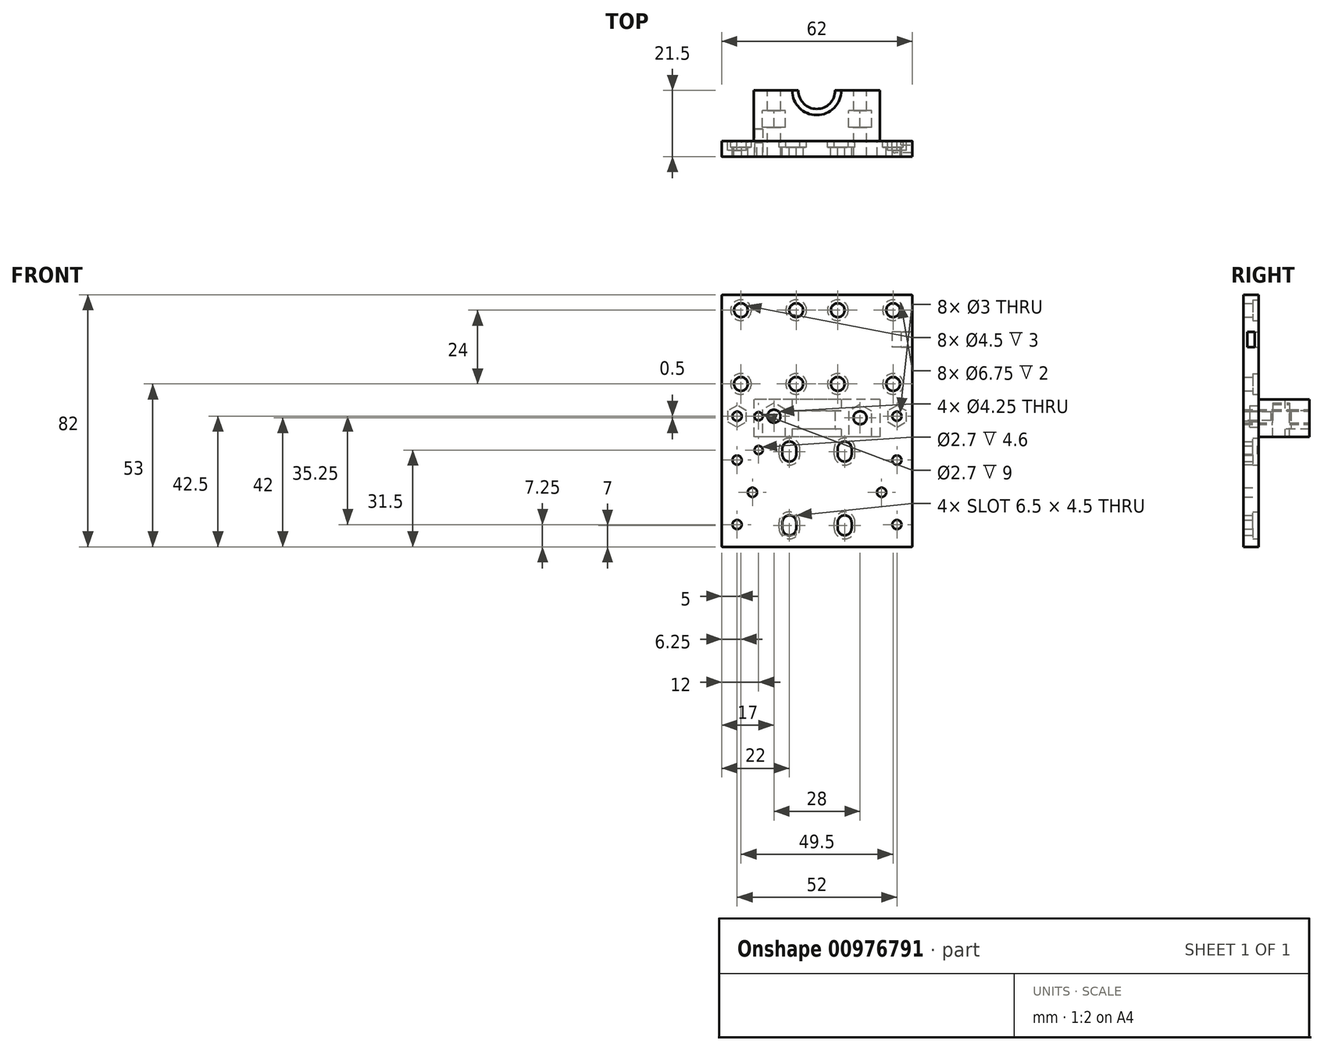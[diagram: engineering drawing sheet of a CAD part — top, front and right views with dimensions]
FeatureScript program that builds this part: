
annotation { "Feature Type Name" : "Feature", "Feature Type Description" : "" }
export const myFeature = defineFeature(function(context is Context, id is Id, definition is map)
    precondition{}
    {
        {
            var Q0;
            Q0=qCreatedBy(makeId("Front.planeOp"),FACE);
            var sketch = newSketch(context, id + "F0", { "sketchPlane" : qUnion([Q0])});
            skLineSegment(sketch, "E0", {"start": v(0, 63.1) * mm, "end": v(0, -63.33) * mm, "construction": true});
            skLineSegment(sketch, "E1", {"start": v(-65.2, 0) * mm, "end": v(78.96, 0) * mm, "construction": true});
            skPoint(sketch, "E2", {"position": v(-24.75, 0) * mm});
            skPoint(sketch, "E3", {"position": v(-6.75, 0) * mm});
            skPoint(sketch, "E4", {"position": v(-6.75, 24) * mm});
            skPoint(sketch, "E5", {"position": v(-24.75, 24) * mm});
            skPoint(sketch, "E6", {"position": v(-26, -10.5) * mm});
            skPoint(sketch, "E7", {"position": v(-19, -10.5) * mm});
            skPoint(sketch, "E8", {"position": v(-19, -21.5) * mm});
            skPoint(sketch, "E9", {"position": v(-9, -21) * mm});
            skPoint(sketch, "E10", {"position": v(-9, -23) * mm});
            skPoint(sketch, "E11", {"position": v(-9, -45) * mm});
            skPoint(sketch, "E12", {"position": v(-9, -47) * mm});
            skCircle(sketch, "E13", {"center": v(-26, -10.5) * mm, "radius": 1.35 * mm});
            skCircle(sketch, "E14", {"center": v(-19, -10.5) * mm, "radius": 1.35 * mm});
            skCircle(sketch, "E15", {"center": v(-19, -21.5) * mm, "radius": 1.35 * mm});
            skCircle(sketch, "E16", {"center": v(-24.75, 24) * mm, "radius": 2.25 * mm});
            skCircle(sketch, "E17", {"center": v(-6.75, 24) * mm, "radius": 2.25 * mm});
            skCircle(sketch, "E18", {"center": v(-24.75, 0) * mm, "radius": 2.25 * mm});
            skCircle(sketch, "E19", {"center": v(-6.75, 0) * mm, "radius": 2.25 * mm});
            skArc(sketch, "E20", {"start": v(-6.75, -21) * mm, "mid": v(-9, -18.75) * mm, "end": v(-11.25, -21) * mm});
            skArc(sketch, "E21", {"start": v(-11.25, -23) * mm, "mid": v(-9, -25.25) * mm, "end": v(-6.75, -23) * mm});
            skLineSegment(sketch, "E22", {"start": v(-6.75, -23) * mm, "end": v(-6.75, -21) * mm});
            skLineSegment(sketch, "E23", {"start": v(-11.25, -23) * mm, "end": v(-11.25, -21) * mm});
            skArc(sketch, "E24", {"start": v(-6.75, -45) * mm, "mid": v(-9, -42.75) * mm, "end": v(-11.25, -45) * mm});
            skArc(sketch, "E25", {"start": v(-11.25, -47) * mm, "mid": v(-9, -49.25) * mm, "end": v(-6.75, -47) * mm});
            skLineSegment(sketch, "E26", {"start": v(-6.75, -47) * mm, "end": v(-6.75, -45) * mm});
            skLineSegment(sketch, "E27", {"start": v(-11.25, -47) * mm, "end": v(-11.25, -45) * mm});
            skLineSegment(sketch, "E28.MirrorCS", {"start": v(11.25, -47) * mm, "end": v(11.25, -45) * mm});
            skLineSegment(sketch, "E29.MirrorCS", {"start": v(11.25, -23) * mm, "end": v(11.25, -21) * mm});
            skArc(sketch, "E30.MirrorCS", {"start": v(11.25, -47) * mm, "mid": v(9, -49.25) * mm, "end": v(6.75, -47) * mm});
            skCircle(sketch, "E31.MirrorC", {"center": v(19, -21.5) * mm, "radius": 1.35 * mm});
            skCircle(sketch, "E32.MirrorC", {"center": v(19, -10.5) * mm, "radius": 1.35 * mm});
            skLineSegment(sketch, "E33.MirrorCS", {"start": v(6.75, -23) * mm, "end": v(6.75, -21) * mm});
            skLineSegment(sketch, "E34.MirrorCS", {"start": v(6.75, -47) * mm, "end": v(6.75, -45) * mm});
            skCircle(sketch, "E35.MirrorC", {"center": v(26, -10.5) * mm, "radius": 1.35 * mm});
            skCircle(sketch, "E36.MirrorC", {"center": v(6.75, 24) * mm, "radius": 2.25 * mm});
            skCircle(sketch, "E37.MirrorC", {"center": v(24.75, 0) * mm, "radius": 2.25 * mm});
            skArc(sketch, "E38.MirrorCS", {"start": v(6.75, -45) * mm, "mid": v(9, -42.75) * mm, "end": v(11.25, -45) * mm});
            skCircle(sketch, "E39.MirrorC", {"center": v(6.75, 0) * mm, "radius": 2.25 * mm});
            skArc(sketch, "E40.MirrorCS", {"start": v(6.75, -21) * mm, "mid": v(9, -18.75) * mm, "end": v(11.25, -21) * mm});
            skArc(sketch, "E41.MirrorCS", {"start": v(11.25, -23) * mm, "mid": v(9, -25.25) * mm, "end": v(6.75, -23) * mm});
            skCircle(sketch, "E42.MirrorC", {"center": v(24.75, 24) * mm, "radius": 2.25 * mm});
            skArc(sketch, "E43.0", {"start": v(5.62, -21) * mm, "mid": v(9, -17.62) * mm, "end": v(12.37, -21) * mm});
            skLineSegment(sketch, "E43.1", {"start": v(5.63, -23) * mm, "end": v(5.63, -21) * mm});
            skArc(sketch, "E43.2", {"start": v(12.37, -23) * mm, "mid": v(9, -26.38) * mm, "end": v(5.62, -23) * mm});
            skLineSegment(sketch, "E43.3", {"start": v(12.38, -23) * mm, "end": v(12.38, -21) * mm});
            skArc(sketch, "E44.0", {"start": v(5.62, -45) * mm, "mid": v(9, -41.62) * mm, "end": v(12.37, -45) * mm});
            skLineSegment(sketch, "E44.1", {"start": v(5.63, -47) * mm, "end": v(5.63, -45) * mm});
            skArc(sketch, "E44.2", {"start": v(12.37, -47) * mm, "mid": v(9, -50.38) * mm, "end": v(5.62, -47) * mm});
            skLineSegment(sketch, "E44.3", {"start": v(12.38, -47) * mm, "end": v(12.38, -45) * mm});
            skArc(sketch, "E45.0", {"start": v(-5.62, -21) * mm, "mid": v(-9, -17.62) * mm, "end": v(-12.37, -21) * mm});
            skLineSegment(sketch, "E45.1", {"start": v(-5.62, -23) * mm, "end": v(-5.62, -21) * mm});
            skArc(sketch, "E45.2", {"start": v(-12.37, -23) * mm, "mid": v(-9, -26.38) * mm, "end": v(-5.62, -23) * mm});
            skLineSegment(sketch, "E45.3", {"start": v(-12.37, -23) * mm, "end": v(-12.37, -21) * mm});
            skArc(sketch, "E46.0", {"start": v(-5.62, -45) * mm, "mid": v(-9, -41.62) * mm, "end": v(-12.37, -45) * mm});
            skLineSegment(sketch, "E46.1", {"start": v(-5.62, -47) * mm, "end": v(-5.62, -45) * mm});
            skArc(sketch, "E46.2", {"start": v(-12.37, -47) * mm, "mid": v(-9, -50.38) * mm, "end": v(-5.62, -47) * mm});
            skLineSegment(sketch, "E46.3", {"start": v(-12.37, -47) * mm, "end": v(-12.37, -45) * mm});
            skPoint(sketch, "E47", {"position": v(26, -24.75) * mm});
            skPoint(sketch, "E48", {"position": v(21, -35.25) * mm});
            skPoint(sketch, "E49", {"position": v(26, -45.75) * mm});
            skPoint(sketch, "E50.MirrorP", {"position": v(-26, -24.75) * mm});
            skPoint(sketch, "E51.MirrorP", {"position": v(-21, -35.25) * mm});
            skPoint(sketch, "E52.MirrorP", {"position": v(-26, -45.75) * mm});
            skSolve(sketch);
        }
        {
            var Q0;
            Q0=qCreatedBy(makeId("Front.planeOp"),FACE);
            var sketch = newSketch(context, id + "F1", { "sketchPlane" : qUnion([Q0])});
            skLineSegment(sketch, "E53.bottom", {"start": v(0, 29) * mm, "end": v(-31, 29) * mm});
            skLineSegment(sketch, "E53.top", {"start": v(0, -53) * mm, "end": v(-31, -53) * mm});
            skLineSegment(sketch, "E53.left", {"start": v(0, 29) * mm, "end": v(0, -53) * mm});
            skLineSegment(sketch, "E53.right", {"start": v(-31, 29) * mm, "end": v(-31, -53) * mm});
            skLineSegment(sketch, "E54.MirrorCS", {"start": v(0, -53) * mm, "end": v(31, -53) * mm});
            skLineSegment(sketch, "E55.MirrorCS", {"start": v(31, 29) * mm, "end": v(31, -53) * mm});
            skLineSegment(sketch, "E56.MirrorCS", {"start": v(0, 29) * mm, "end": v(31, 29) * mm});
            skSolve(sketch);
        }
        {
            var Q0;
            Q0 = qSketchRegion(id + "F1", true);
            extrude(context, id + "F2", {"entities" : qUnion([Q0]), "depth" : 5 * mm, "offsetDistance" : 25 * mm});
        }
        {
            var Q0;
            Q0=sQuery(id+"F0.wireOp",VERTEX,"E42.MirrorC.center");
            var Q1;
            Q1=sQuery(id+"F0.wireOp",VERTEX,"E36.MirrorC.center");
            var Q2;
            Q2=sQuery(id+"F0.wireOp",VERTEX,"E4");
            var Q3;
            Q3=sQuery(id+"F0.wireOp",VERTEX,"E5");
            var Q4;
            Q4=sQuery(id+"F0.wireOp",VERTEX,"E2");
            var Q5;
            Q5=sQuery(id+"F0.wireOp",VERTEX,"E3");
            var Q6;
            Q6=sQuery(id+"F0.wireOp",VERTEX,"E39.MirrorC.center");
            var Q7;
            Q7=sQuery(id+"F0.wireOp",VERTEX,"E37.MirrorC.center");
            var Q8;
            Q8=makeQuery(id+"F2.opExtrude","SWEPT_BODY",BODY,{"disambiguationData":[OSD([sQuery(id+"F1.wireOp",EDGE,"E53.bottom"),sQuery(id+"F1.wireOp",EDGE,"E53.top"),sQuery(id+"F1.wireOp",EDGE,"E53.right"),sQuery(id+"F1.wireOp",EDGE,"E54.MirrorCS"),sQuery(id+"F1.wireOp",EDGE,"E55.MirrorCS"),sQuery(id+"F1.wireOp",EDGE,"E56.MirrorCS")])]});
            hole(context, id + "F3", {"style" : HoleStyle.C_BORE, "endStyle" : HoleEndStyle.THROUGH, "oppositeDirection" : true, "holeDiameter" : 4.5 * mm, "cBoreDiameter" : 6.75 * mm, "cBoreDepth" : 2 * mm, "majorDiameter" : 5 * mm, "isTappedThrough" : true, "tappedDepth" : 15 * mm, "tapClearance" : 3, "locations" : qUnion([Q0, Q1, Q2, Q3, Q4, Q5, Q6, Q7]), "scope" : qUnion([Q8])});
        }
        {
            var Q0;
            Q0=makeQuery(id+"F0.imprint","IMPRINT",FACE,{"disambiguationData":[TD([[makeQuery(id+"F0.imprint","IMPRINT",EDGE,{"derivedFrom":sQuery(id+"F0.wireOp",EDGE,"E29.MirrorCS")}),1.0]])]});
            var Q1;
            Q1=makeQuery(id+"F0.imprint","IMPRINT",FACE,{"disambiguationData":[TD([[makeQuery(id+"F0.imprint","IMPRINT",EDGE,{"derivedFrom":sQuery(id+"F0.wireOp",EDGE,"E20")}),1.0]])]});
            var Q2;
            Q2=makeQuery(id+"F0.imprint","IMPRINT",FACE,{"disambiguationData":[TD([[makeQuery(id+"F0.imprint","IMPRINT",EDGE,{"derivedFrom":sQuery(id+"F0.wireOp",EDGE,"E28.MirrorCS")}),1.0]])]});
            var Q3;
            Q3=makeQuery(id+"F0.imprint","IMPRINT",FACE,{"disambiguationData":[TD([[makeQuery(id+"F0.imprint","IMPRINT",EDGE,{"derivedFrom":sQuery(id+"F0.wireOp",EDGE,"E24")}),1.0]])]});
            extrude(context, id + "F4", {"entities" : qUnion([Q0, Q1, Q2, Q3]), "operationType" : NewBodyOperationType.REMOVE, "endBound" : BoundingType.UP_TO_NEXT, "depth" : 25 * mm, "offsetDistance" : 25 * mm});
        }
        {
            var Q0;
            Q0=makeQuery(id+"F0.imprint","IMPRINT",FACE,{"disambiguationData":[TD([[makeQuery(id+"F0.imprint","IMPRINT",EDGE,{"derivedFrom":sQuery(id+"F0.wireOp",EDGE,"E29.MirrorCS")}),-1.0]])]});
            var Q1;
            Q1=makeQuery(id+"F0.imprint","IMPRINT",FACE,{"disambiguationData":[TD([[makeQuery(id+"F0.imprint","IMPRINT",EDGE,{"derivedFrom":sQuery(id+"F0.wireOp",EDGE,"E20")}),-1.0]])]});
            var Q2;
            Q2=makeQuery(id+"F0.imprint","IMPRINT",FACE,{"disambiguationData":[TD([[makeQuery(id+"F0.imprint","IMPRINT",EDGE,{"derivedFrom":sQuery(id+"F0.wireOp",EDGE,"E24")}),-1.0]])]});
            var Q3;
            Q3=makeQuery(id+"F0.imprint","IMPRINT",FACE,{"disambiguationData":[TD([[makeQuery(id+"F0.imprint","IMPRINT",EDGE,{"derivedFrom":sQuery(id+"F0.wireOp",EDGE,"E28.MirrorCS")}),-1.0]])]});
            extrude(context, id + "F5", {"entities" : qUnion([Q0, Q1, Q2, Q3]), "operationType" : NewBodyOperationType.REMOVE, "depth" : 2 * mm, "offsetDistance" : 25 * mm});
        }
        {
            var Q0;
            Q0=makeQuery(id+"F0.imprint","IMPRINT",FACE,{"disambiguationData":[TD([[makeQuery(id+"F0.imprint","IMPRINT",EDGE,{"derivedFrom":sQuery(id+"F0.wireOp",EDGE,"E15")}),1.0]])]});
            var Q1;
            Q1=makeQuery(id+"F0.imprint","IMPRINT",FACE,{"disambiguationData":[TD([[makeQuery(id+"F0.imprint","IMPRINT",EDGE,{"derivedFrom":sQuery(id+"F0.wireOp",EDGE,"E31.MirrorC")}),-1.0]])]});
            var Q2;
            Q2=sQuery(id+"F0.wireOp",EDGE,"E35.MirrorC");
            var Q3;
            Q3=sQuery(id+"F0.wireOp",EDGE,"E32.MirrorC");
            var Q4;
            Q4=sQuery(id+"F0.wireOp",EDGE,"E31.MirrorC");
            var Q5;
            Q5=sQuery(id+"F0.wireOp",EDGE,"E15");
            var Q6;
            Q6=sQuery(id+"F0.wireOp",EDGE,"E14");
            var Q7;
            Q7=sQuery(id+"F0.wireOp",EDGE,"E13");
            extrude(context, id + "F6", {"entities" : qUnion([Q0, Q1]), "operationType" : NewBodyOperationType.REMOVE, "surfaceEntities" : qUnion([Q2, Q3, Q4, Q5, Q6, Q7]), "endBound" : BoundingType.THROUGH_ALL, "depth" : 1 * mm, "offsetDistance" : 25 * mm, "hasSecondDirection" : true, "secondDirectionOppositeDirection" : false, "secondDirectionDepth" : 0.4 * mm});
        }
        {
            var Q0;
            Q0=sQuery(id+"F0.wireOp",VERTEX,"E35.MirrorC.center");
            var Q1;
            Q1=sQuery(id+"F0.wireOp",VERTEX,"E6");
            var Q2;
            Q2=makeQuery(id+"F2.opExtrude","SWEPT_BODY",BODY,{"disambiguationData":[OSD([sQuery(id+"F1.wireOp",EDGE,"E53.bottom"),sQuery(id+"F1.wireOp",EDGE,"E53.top"),sQuery(id+"F1.wireOp",EDGE,"E53.right"),sQuery(id+"F1.wireOp",EDGE,"E54.MirrorCS"),sQuery(id+"F1.wireOp",EDGE,"E55.MirrorCS"),sQuery(id+"F1.wireOp",EDGE,"E56.MirrorCS")])]});
            hole(context, id + "F7", {"style" : HoleStyle.SIMPLE, "endStyle" : HoleEndStyle.THROUGH, "oppositeDirection" : true, "holeDiameter" : 3 * mm, "majorDiameter" : 5 * mm, "isTappedThrough" : true, "tappedDepth" : 15 * mm, "tapClearance" : 3, "locations" : qUnion([Q0, Q1]), "scope" : qUnion([Q2])});
        }
        {
            var Q0;
            Q0=makeQuery(id+"F2.opExtrude","CAP_FACE",FACE,{"disambiguationData":[OSD([sQuery(id+"F1.wireOp",EDGE,"E53.bottom"),sQuery(id+"F1.wireOp",EDGE,"E53.top"),sQuery(id+"F1.wireOp",EDGE,"E53.right"),sQuery(id+"F1.wireOp",EDGE,"E54.MirrorCS"),sQuery(id+"F1.wireOp",EDGE,"E55.MirrorCS"),sQuery(id+"F1.wireOp",EDGE,"E56.MirrorCS")])],"isStart":true});
            var sketch = newSketch(context, id + "F8", { "sketchPlane" : qUnion([Q0])});
            skPoint(sketch, "E57.0", {"position": v(-26, -10.5) * mm});
            skPoint(sketch, "E58.0", {"position": v(26, -10.5) * mm});
            skCircle(sketch, "E59.cCircle", {"center": v(-26, -10.5) * mm, "radius": 3.02 * mm, "construction": true});
            skLineSegment(sketch, "E59.0", {"start": v(-22.97, -8.75) * mm, "end": v(-22.97, -12.25) * mm});
            skLineSegment(sketch, "E59.1", {"start": v(-22.97, -12.25) * mm, "end": v(-26, -14) * mm});
            skLineSegment(sketch, "E59.2", {"start": v(-26, -14) * mm, "end": v(-29.02, -12.25) * mm});
            skLineSegment(sketch, "E59.3", {"start": v(-29.02, -12.25) * mm, "end": v(-29.02, -8.75) * mm});
            skLineSegment(sketch, "E59.4", {"start": v(-29.02, -8.75) * mm, "end": v(-26, -7) * mm});
            skLineSegment(sketch, "E59.5", {"start": v(-26, -7) * mm, "end": v(-22.97, -8.75) * mm});
            skPoint(sketch, "E59.0.midPoint", {"position": v(-22.97, -10.5) * mm});
            skCircle(sketch, "E60.cCircle", {"center": v(26, -10.5) * mm, "radius": 3.02 * mm, "construction": true});
            skLineSegment(sketch, "E60.0", {"start": v(29.02, -8.75) * mm, "end": v(29.02, -12.25) * mm});
            skLineSegment(sketch, "E60.1", {"start": v(29.02, -12.25) * mm, "end": v(26, -14) * mm});
            skLineSegment(sketch, "E60.2", {"start": v(26, -14) * mm, "end": v(22.97, -12.25) * mm});
            skLineSegment(sketch, "E60.3", {"start": v(22.97, -12.25) * mm, "end": v(22.97, -8.75) * mm});
            skLineSegment(sketch, "E60.4", {"start": v(22.97, -8.75) * mm, "end": v(26, -7) * mm});
            skLineSegment(sketch, "E60.5", {"start": v(26, -7) * mm, "end": v(29.02, -8.75) * mm});
            skPoint(sketch, "E60.0.midPoint", {"position": v(29.02, -10.5) * mm});
            skSolve(sketch);
        }
        {
            var Q0;
            Q0=makeQuery(id+"F8.imprint","IMPRINT",FACE,{"disambiguationData":[TD([[makeQuery(id+"F8.imprint","IMPRINT",EDGE,{"derivedFrom":sQuery(id+"F8.wireOp",EDGE,"E60.0")}),-1.0]])]});
            var Q1;
            Q1=makeQuery(id+"F8.imprint","IMPRINT",FACE,{"disambiguationData":[TD([[makeQuery(id+"F8.imprint","IMPRINT",EDGE,{"derivedFrom":sQuery(id+"F8.wireOp",EDGE,"E59.0")}),-1.0]])]});
            extrude(context, id + "F9", {"entities" : qUnion([Q0, Q1]), "operationType" : NewBodyOperationType.REMOVE, "oppositeDirection" : true, "depth" : 3 * mm, "offsetDistance" : 25 * mm});
        }
        {
            var Q0;
            Q0=makeQuery(id+"F2.opExtrude","CAP_FACE",FACE,{"disambiguationData":[OSD([sQuery(id+"F1.wireOp",EDGE,"E53.bottom"),sQuery(id+"F1.wireOp",EDGE,"E53.top"),sQuery(id+"F1.wireOp",EDGE,"E53.right"),sQuery(id+"F1.wireOp",EDGE,"E54.MirrorCS"),sQuery(id+"F1.wireOp",EDGE,"E55.MirrorCS"),sQuery(id+"F1.wireOp",EDGE,"E56.MirrorCS")])],"isStart":true});
            var sketch = newSketch(context, id + "F10", { "sketchPlane" : qUnion([Q0])});
            skLineSegment(sketch, "E61.bottom", {"start": v(-20.4, -5) * mm, "end": v(0.1, -5) * mm});
            skLineSegment(sketch, "E61.top", {"start": v(-20.4, -17.25) * mm, "end": v(-7.9, -17.25) * mm});
            skLineSegment(sketch, "E61.left", {"start": v(-20.4, -5) * mm, "end": v(-20.4, -17.25) * mm});
            skLineSegment(sketch, "E61.right", {"start": v(20.6, -5) * mm, "end": v(20.6, -17.25) * mm});
            skLineSegment(sketch, "E62", {"start": v(0.1, -2.78) * mm, "end": v(0.1, -28.46) * mm, "construction": true});
            skLineSegment(sketch, "E63", {"start": v(-7.9, -5) * mm, "end": v(-7.9, -8.7) * mm});
            skLineSegment(sketch, "E64", {"start": v(-7.9, -8.7) * mm, "end": v(-5.9, -8.7) * mm});
            skLineSegment(sketch, "E65", {"start": v(-5.9, -8.7) * mm, "end": v(-5.9, -14.7) * mm});
            skLineSegment(sketch, "E66", {"start": v(-5.9, -14.7) * mm, "end": v(-7.9, -14.7) * mm});
            skLineSegment(sketch, "E67", {"start": v(-7.9, -14.7) * mm, "end": v(-7.9, -17.25) * mm});
            skLineSegment(sketch, "E68", {"start": v(1.38, -5) * mm, "end": v(20.6, -5) * mm});
            skLineSegment(sketch, "E69", {"start": v(0.1, -5) * mm, "end": v(1.38, -5) * mm});
            skLineSegment(sketch, "E70", {"start": v(0.1, -17.25) * mm, "end": v(20.6, -17.25) * mm});
            skLineSegment(sketch, "E71", {"start": v(-7.9, -17.25) * mm, "end": v(0.1, -17.25) * mm});
            skSolve(sketch);
        }
        {
            var Q0;
            Q0=makeQuery(id+"F10.imprint","IMPRINT",FACE,{"disambiguationData":[TD([[makeQuery(id+"F10.imprint","IMPRINT",EDGE,{"derivedFrom":sQuery(id+"F10.wireOp",EDGE,"E61.top")}),1.0]])]});
            var Q1;
            Q1=makeQuery(id+"F10.imprint","IMPRINT",FACE,{"disambiguationData":[TD([[makeQuery(id+"F10.imprint","IMPRINT",EDGE,{"derivedFrom":sQuery(id+"F10.wireOp",EDGE,"E61.right")}),-1.0]])]});
            extrude(context, id + "F11", {"entities" : qUnion([Q0, Q1]), "operationType" : NewBodyOperationType.ADD, "depth" : 16.5 * mm, "offsetDistance" : 25 * mm});
        }
        {
            var Q0;
            Q0=makeQuery(id+"F11.opExtrude","CAP_FACE",FACE,{"disambiguationData":[OSD([sQuery(id+"F10.wireOp",EDGE,"E61.bottom"),sQuery(id+"F10.wireOp",EDGE,"E61.top"),sQuery(id+"F10.wireOp",EDGE,"E61.left"),sQuery(id+"F10.wireOp",EDGE,"E61.right"),sQuery(id+"F10.wireOp",EDGE,"E68"),sQuery(id+"F10.wireOp",EDGE,"E69"),sQuery(id+"F10.wireOp",EDGE,"E70"),sQuery(id+"F10.wireOp",EDGE,"E71")])],"isStart":false});
            var sketch = newSketch(context, id + "F12", { "sketchPlane" : qUnion([Q0])});
            skLineSegment(sketch, "E72.0", {"start": v(-20.4, -5) * mm, "end": v(-20.4, -17.25) * mm});
            skLineSegment(sketch, "E73.0", {"start": v(20.6, -5) * mm, "end": v(20.6, -17.25) * mm});
            skLineSegment(sketch, "E74", {"start": v(0.1, -3.2) * mm, "end": v(0.1, -20.42) * mm, "construction": true});
            skLineSegment(sketch, "E75", {"start": v(0.1, -5) * mm, "end": v(-7.9, -5) * mm});
            skLineSegment(sketch, "E76", {"start": v(-7.9, -5) * mm, "end": v(-7.9, -8.7) * mm});
            skLineSegment(sketch, "E77", {"start": v(-7.9, -8.7) * mm, "end": v(-5.9, -8.7) * mm});
            skLineSegment(sketch, "E78", {"start": v(-5.9, -8.7) * mm, "end": v(-5.9, -14.7) * mm});
            skLineSegment(sketch, "E79", {"start": v(-5.9, -14.7) * mm, "end": v(-7.9, -14.7) * mm});
            skLineSegment(sketch, "E80", {"start": v(-7.9, -14.7) * mm, "end": v(-7.9, -17.25) * mm});
            skLineSegment(sketch, "E81", {"start": v(-7.9, -17.25) * mm, "end": v(0.1, -17.25) * mm});
            skLineSegment(sketch, "E82", {"start": v(0.1, -5) * mm, "end": v(0.1, -17.25) * mm});
            skSolve(sketch);
        }
        {
            var Q0;
            Q0=makeQuery(id+"F12.imprint","IMPRINT",FACE,{"disambiguationData":[TD([[makeQuery(id+"F12.imprint","IMPRINT",EDGE,{"derivedFrom":sQuery(id+"F12.wireOp",EDGE,"E75")}),-1.0]])]});
            var Q1;
            Q1=sQuery(id+"F12.wireOp",EDGE,"E74");
            revolve(context, id + "F13", {"operationType" : NewBodyOperationType.REMOVE, "surfaceOperationType" : NewSurfaceOperationType.NEW, "entities" : qUnion([Q0]), "axis" : qUnion([Q1]), "revolveType" : RevolveType.FULL, "oppositeDirection" : true});
        }
        {
            var Q0;
            {var subQ0=sQuery(id+"F10.wireOp",EDGE,"E61.left");var subQ1=sQuery(id+"F10.wireOp",EDGE,"E71");var subQ2=sQuery(id+"F10.wireOp",EDGE,"E70");var subQ3=sQuery(id+"F10.wireOp",EDGE,"E61.top");var subQ4=sQuery(id+"F10.wireOp",EDGE,"E69");var subQ5=sQuery(id+"F10.wireOp",EDGE,"E68");var subQ6=sQuery(id+"F10.wireOp",EDGE,"E61.bottom");Q0=makeQuery(id+"F13.boolean.opBoolean","SPLIT",FACE,{"disambiguationData":[TD([makeQuery(id+"F11.opExtrude","SWEPT_FACE",FACE,{"disambiguationData":[OSD([subQ0])]})])],"derivedFrom":makeQuery(id+"F11.opExtrude","CAP_FACE",FACE,{"disambiguationData":[OSD([subQ6,subQ3,subQ0,sQuery(id+"F10.wireOp",EDGE,"E61.right"),subQ5,subQ4,subQ2,subQ1])],"isStart":false})});}
            var sketch = newSketch(context, id + "F14", { "sketchPlane" : qUnion([Q0])});
            skPoint(sketch, "E83", {"position": v(-14, -11) * mm});
            skPoint(sketch, "E84", {"position": v(14, -10.5) * mm});
            skSolve(sketch);
        }
        {
            var Q0;
            Q0=sQuery(id+"F14.wireOp",VERTEX,"E83");
            var Q1;
            Q1=sQuery(id+"F14.wireOp",VERTEX,"E84");
            var Q2;
            Q2=makeQuery(id+"F2.opExtrude","SWEPT_BODY",BODY,{"disambiguationData":[OSD([sQuery(id+"F1.wireOp",EDGE,"E53.bottom"),sQuery(id+"F1.wireOp",EDGE,"E53.top"),sQuery(id+"F1.wireOp",EDGE,"E53.right"),sQuery(id+"F1.wireOp",EDGE,"E54.MirrorCS"),sQuery(id+"F1.wireOp",EDGE,"E55.MirrorCS"),sQuery(id+"F1.wireOp",EDGE,"E56.MirrorCS")])]});
            hole(context, id + "F15", {"style" : HoleStyle.SIMPLE, "endStyle" : HoleEndStyle.THROUGH, "holeDiameter" : 4.25 * mm, "majorDiameter" : 5 * mm, "isTappedThrough" : true, "tappedDepth" : 15 * mm, "tapClearance" : 3, "locations" : qUnion([Q0, Q1]), "scope" : qUnion([Q2])});
        }
        {
            var Q0;
            Q0=sQuery(id+"F0.wireOp",VERTEX,"E47");
            var Q1;
            Q1=sQuery(id+"F0.wireOp",VERTEX,"E48");
            var Q2;
            Q2=sQuery(id+"F0.wireOp",VERTEX,"E49");
            var Q3;
            Q3=sQuery(id+"F0.wireOp",VERTEX,"E51.MirrorP");
            var Q4;
            Q4=sQuery(id+"F0.wireOp",VERTEX,"E50.MirrorP");
            var Q5;
            Q5=sQuery(id+"F0.wireOp",VERTEX,"E52.MirrorP");
            var Q6;
            Q6=makeQuery(id+"F2.opExtrude","SWEPT_BODY",BODY,{"disambiguationData":[OSD([sQuery(id+"F1.wireOp",EDGE,"E53.bottom"),sQuery(id+"F1.wireOp",EDGE,"E53.top"),sQuery(id+"F1.wireOp",EDGE,"E53.right"),sQuery(id+"F1.wireOp",EDGE,"E54.MirrorCS"),sQuery(id+"F1.wireOp",EDGE,"E55.MirrorCS"),sQuery(id+"F1.wireOp",EDGE,"E56.MirrorCS")])]});
            hole(context, id + "F16", {"style" : HoleStyle.SIMPLE, "endStyle" : HoleEndStyle.THROUGH, "oppositeDirection" : true, "holeDiameter" : 3 * mm, "majorDiameter" : 5 * mm, "isTappedThrough" : true, "tappedDepth" : 15 * mm, "tapClearance" : 3, "locations" : qUnion([Q0, Q1, Q2, Q3, Q4, Q5]), "scope" : qUnion([Q6])});
        }
        {
            var Q0;
            {var subQ0=sQuery(id+"F10.wireOp",EDGE,"E61.left");var subQ1=sQuery(id+"F10.wireOp",EDGE,"E71");var subQ2=sQuery(id+"F10.wireOp",EDGE,"E70");var subQ3=sQuery(id+"F10.wireOp",EDGE,"E61.top");var subQ4=sQuery(id+"F10.wireOp",EDGE,"E69");var subQ5=sQuery(id+"F10.wireOp",EDGE,"E68");var subQ6=sQuery(id+"F10.wireOp",EDGE,"E61.bottom");Q0=makeQuery(id+"F13.boolean.opBoolean","SPLIT",FACE,{"disambiguationData":[TD([makeQuery(id+"F11.opExtrude","SWEPT_FACE",FACE,{"disambiguationData":[OSD([subQ0])]})])],"derivedFrom":makeQuery(id+"F11.opExtrude","CAP_FACE",FACE,{"disambiguationData":[OSD([subQ6,subQ3,subQ0,sQuery(id+"F10.wireOp",EDGE,"E61.right"),subQ5,subQ4,subQ2,subQ1])],"isStart":false})});}
            cPlane(context, id + "F17", {"entities" : qUnion([Q0]), "cplaneType" : CPlaneType.OFFSET, "offset" : 6.5 * mm, "oppositeDirection" : true, "width" : 150 * mm, "height" : 150 * mm});
        }
        {
            var Q0;
            Q0=qCreatedBy(id+"F17.planeOp",FACE);
            var sketch = newSketch(context, id + "F18", { "sketchPlane" : qUnion([Q0])});
            skCircle(sketch, "E85.0", {"center": v(-14, -11) * mm, "radius": 2.12 * mm});
            skCircle(sketch, "E86.0", {"center": v(14, -10.5) * mm, "radius": 2.12 * mm});
            skArc(sketch, "E87.cCircle", {"start": v(-12.12, -14.25) * mm, "mid": v(-14, -7.25) * mm, "end": v(-15.88, -14.25) * mm, "construction": true});
            skLineSegment(sketch, "E87.0", {"start": v(-10.25, -8.83) * mm, "end": v(-10.25, -13.17) * mm});
            skLineSegment(sketch, "E87.3", {"start": v(-17.75, -13.17) * mm, "end": v(-17.75, -8.83) * mm});
            skLineSegment(sketch, "E87.4", {"start": v(-17.75, -8.83) * mm, "end": v(-14, -6.67) * mm});
            skLineSegment(sketch, "E87.5", {"start": v(-14, -6.67) * mm, "end": v(-10.25, -8.83) * mm});
            skPoint(sketch, "E87.0.midPoint", {"position": v(-10.25, -11) * mm});
            skCircle(sketch, "E88.cCircle", {"center": v(14, -10.5) * mm, "radius": 3.75 * mm, "construction": true});
            skLineSegment(sketch, "E88.0", {"start": v(17.75, -8.33) * mm, "end": v(17.75, -12.67) * mm});
            skLineSegment(sketch, "E88.3", {"start": v(10.25, -12.67) * mm, "end": v(10.25, -8.33) * mm});
            skLineSegment(sketch, "E88.4", {"start": v(10.25, -8.33) * mm, "end": v(14, -6.17) * mm});
            skLineSegment(sketch, "E88.5", {"start": v(14, -6.17) * mm, "end": v(17.75, -8.33) * mm});
            skPoint(sketch, "E88.0.midPoint", {"position": v(17.75, -10.5) * mm});
            skLineSegment(sketch, "E89.0", {"start": v(-20.4, -17.25) * mm, "end": v(20.6, -17.25) * mm});
            skLineSegment(sketch, "E90.top", {"start": v(-17.75, -17.25) * mm, "end": v(-10.25, -17.25) * mm});
            skLineSegment(sketch, "E90.left", {"start": v(-17.75, -13.17) * mm, "end": v(-17.75, -17.25) * mm});
            skLineSegment(sketch, "E90.right", {"start": v(-10.25, -13.17) * mm, "end": v(-10.25, -17.25) * mm});
            skLineSegment(sketch, "E91.top", {"start": v(10.25, -17.25) * mm, "end": v(17.75, -17.25) * mm});
            skLineSegment(sketch, "E91.left", {"start": v(10.25, -12.67) * mm, "end": v(10.25, -17.25) * mm});
            skLineSegment(sketch, "E91.right", {"start": v(17.75, -12.67) * mm, "end": v(17.75, -17.25) * mm});
            skPoint(sketch, "E92.orphan", {"position": v(14, -14.83) * mm});
            skSolve(sketch);
        }
        {
            var Q0;
            Q0 = qSketchRegion(id + "F18", true);
            extrude(context, id + "F19", {"entities" : qUnion([Q0]), "operationType" : NewBodyOperationType.REMOVE, "oppositeDirection" : true, "depth" : 5.5 * mm, "offsetDistance" : 25 * mm});
        }
        {
            var Q0;
            Q0=makeQuery(id+"F2.opExtrude","CAP_FACE",FACE,{"disambiguationData":[OSD([sQuery(id+"F1.wireOp",EDGE,"E53.bottom"),sQuery(id+"F1.wireOp",EDGE,"E53.top"),sQuery(id+"F1.wireOp",EDGE,"E53.right"),sQuery(id+"F1.wireOp",EDGE,"E54.MirrorCS"),sQuery(id+"F1.wireOp",EDGE,"E55.MirrorCS"),sQuery(id+"F1.wireOp",EDGE,"E56.MirrorCS")])],"isStart":true});
            var sketch = newSketch(context, id + "F20", { "sketchPlane" : qUnion([Q0])});
            skLineSegment(sketch, "E93.bottom", {"start": v(-27.35, 16.98) * mm, "end": v(-24.35, 16.98) * mm});
            skLineSegment(sketch, "E93.top", {"start": v(-27.35, 11.98) * mm, "end": v(-24.35, 11.98) * mm});
            skLineSegment(sketch, "E93.left", {"start": v(-27.35, 16.98) * mm, "end": v(-27.35, 11.98) * mm});
            skLineSegment(sketch, "E93.right", {"start": v(-24.35, 16.98) * mm, "end": v(-24.35, 11.98) * mm});
            skLineSegment(sketch, "E94.MirrorCS", {"start": v(27.35, 16.98) * mm, "end": v(27.35, 11.98) * mm});
            skLineSegment(sketch, "E95.MirrorCS", {"start": v(24.35, 16.98) * mm, "end": v(24.35, 11.98) * mm});
            skLineSegment(sketch, "E96.MirrorCS", {"start": v(27.35, 11.98) * mm, "end": v(24.35, 11.98) * mm});
            skLineSegment(sketch, "E97.MirrorCS", {"start": v(27.35, 16.98) * mm, "end": v(24.35, 16.98) * mm});
            skSolve(sketch);
        }
        {
            var Q0;
            Q0=makeQuery(id+"F20.imprint","IMPRINT",FACE,{"disambiguationData":[TD([[makeQuery(id+"F20.imprint","IMPRINT",EDGE,{"derivedFrom":sQuery(id+"F20.wireOp",EDGE,"E93.bottom")}),-1.0]])]});
            extrude(context, id + "F21", {"entities" : qUnion([Q0]), "operationType" : NewBodyOperationType.REMOVE, "oppositeDirection" : true, "depth" : 3.75 * mm, "offsetDistance" : 25 * mm});
        }
        {
            var Q0;
            Q0=makeQuery(id+"F2.opExtrude","SWEPT_FACE",FACE,{"disambiguationData":[OSD([sQuery(id+"F1.wireOp",EDGE,"E55.MirrorCS")])]});
            var sketch = newSketch(context, id + "F22", { "sketchPlane" : qUnion([Q0])});
            skLineSegment(sketch, "E98.0.0", {"start": v(0, 11.98) * mm, "end": v(0, 16.98) * mm});
            skLineSegment(sketch, "E98.0.1", {"start": v(0, 16.98) * mm, "end": v(-3.75, 16.98) * mm});
            skLineSegment(sketch, "E98.0.2", {"start": v(-3.75, 16.98) * mm, "end": v(-3.75, 11.98) * mm});
            skLineSegment(sketch, "E98.0.3", {"start": v(-3.75, 11.98) * mm, "end": v(0, 11.98) * mm});
            skLineSegment(sketch, "E99.bottom", {"start": v(-3.75, 16.98) * mm, "end": v(-1.25, 16.98) * mm});
            skLineSegment(sketch, "E99.top", {"start": v(-3.75, 11.98) * mm, "end": v(-1.25, 11.98) * mm});
            skLineSegment(sketch, "E99.right", {"start": v(-1.25, 16.98) * mm, "end": v(-1.25, 11.98) * mm});
            skSolve(sketch);
        }
        {
            var Q0;
            {var subQ2=sQuery(id+"F22.wireOp",EDGE,"E98.0.2");Q0=makeQuery(id+"F22.imprint","IMPRINT",FACE,{"disambiguationData":[TD([[makeQuery(id+"F22.imprint","IMPRINT",EDGE,{"derivedFrom":subQ2}),1.0]])]});}
            extrude(context, id + "F23", {"entities" : qUnion([Q0]), "operationType" : NewBodyOperationType.REMOVE, "endBound" : BoundingType.UP_TO_NEXT, "oppositeDirection" : true, "depth" : 25 * mm, "offsetDistance" : 25 * mm});
        }
        {
            var Q0;
            Q0=makeQuery(id+"F21.boolean.opBoolean","COPY",EDGE,{"derivedFrom":makeQuery(id+"F21.opExtrude","CAP_EDGE",EDGE,{"disambiguationData":[OSD([sQuery(id+"F20.wireOp",EDGE,"E93.right")])],"isStart":false})});
            var Q1;
            Q1=makeQuery(id+"F23.boolean.opBoolean","COPY",EDGE,{"derivedFrom":makeQuery(id+"F23.opExtrude","CAP_EDGE",EDGE,{"disambiguationData":[OSD([sQuery(id+"F22.wireOp",EDGE,"E99.right")])],"isStart":false})});
            fillet(context, id + "F24", {"entities" : qUnion([Q0, Q1]), "radius" : 1 * mm, "tangentPropagation" : true, "allowEdgeOverflow" : false});
        }
        {
            var Q0;
            Q0=makeQuery(id+"F0.imprint","IMPRINT",FACE,{"disambiguationData":[TD([[makeQuery(id+"F0.imprint","IMPRINT",EDGE,{"derivedFrom":sQuery(id+"F0.wireOp",EDGE,"E14")}),1.0]])]});
            var Q1;
            Q1=makeQuery(id+"F0.imprint","IMPRINT",FACE,{"disambiguationData":[TD([[makeQuery(id+"F0.imprint","IMPRINT",EDGE,{"derivedFrom":sQuery(id+"F0.wireOp",EDGE,"E32.MirrorC")}),-1.0]])]});
            var Q2;
            Q2=sQuery(id+"F0.wireOp",EDGE,"E14");
            var Q3;
            Q3=sQuery(id+"F0.wireOp",EDGE,"E32.MirrorC");
            extrude(context, id + "F25", {"entities" : qUnion([Q0, Q1]), "operationType" : NewBodyOperationType.REMOVE, "surfaceEntities" : qUnion([Q2, Q3]), "oppositeDirection" : true, "depth" : 4 * mm, "offsetDistance" : 25 * mm, "hasSecondDirection" : true, "secondDirectionBound" : SecondDirectionBoundingType.THROUGH_ALL, "secondDirectionOppositeDirection" : false, "secondDirectionDepth" : 25 * mm});
        }
        {
            var Q0;
            Q0=makeQuery(id+"F2.opExtrude","SWEPT_EDGE",EDGE,{"disambiguationData":[OSD([sQuery(id+"F1.wireOp",EDGE,"E53.bottom"),sQuery(id+"F1.wireOp",EDGE,"E53.right")])]});
            var Q1;
            Q1=makeQuery(id+"F2.opExtrude","SWEPT_EDGE",EDGE,{"disambiguationData":[OSD([sQuery(id+"F1.wireOp",EDGE,"E55.MirrorCS"),sQuery(id+"F1.wireOp",EDGE,"E56.MirrorCS")])]});
            var Q2;
            Q2=makeQuery(id+"F2.opExtrude","SWEPT_EDGE",EDGE,{"disambiguationData":[OSD([sQuery(id+"F1.wireOp",EDGE,"E54.MirrorCS"),sQuery(id+"F1.wireOp",EDGE,"E55.MirrorCS")])]});
            var Q3;
            Q3=makeQuery(id+"F2.opExtrude","SWEPT_EDGE",EDGE,{"disambiguationData":[OSD([sQuery(id+"F1.wireOp",EDGE,"E53.top"),sQuery(id+"F1.wireOp",EDGE,"E53.right")])]});
            var Q4;
            Q4=makeQuery(id+"F13.boolean.opBoolean","COPY",EDGE,{"derivedFrom":makeQuery(id+"F13.opRevolve","SWEPT_EDGE",EDGE,{"disambiguationData":[OSD([sQuery(id+"F12.wireOp",EDGE,"E77"),sQuery(id+"F12.wireOp",EDGE,"E78")])]})});
            var Q5;
            Q5=makeQuery(id+"F13.boolean.opBoolean","COPY",EDGE,{"derivedFrom":makeQuery(id+"F13.opRevolve","SWEPT_EDGE",EDGE,{"disambiguationData":[OSD([sQuery(id+"F12.wireOp",EDGE,"E78"),sQuery(id+"F12.wireOp",EDGE,"E79")])]})});
            fillet(context, id + "F26", {"entities" : qUnion([Q0, Q1, Q2, Q3, Q4, Q5]), "radius" : 0.3 * mm, "tangentPropagation" : true, "allowEdgeOverflow" : false});
        }
    });
